# Revit family: FT6
name_source: partatom
category: Lighting Fixtures
revit_build: Autodesk Revit 2014 (Build: 20130308_1515(x64)
units: mm (PartAtom-declared; Revit-internal decimal feet)

## types (1)
- FT6
    Apparent Load = 0 VA
    Assembly Code = D5020210
    Color Filter = 16777215
    Default Elevation = 22"
    Description = 6'' Incandescent Fire-Resistant Downlights
    Dimming Lamp Color Temperature Shift = <None>
    Emit Shape Visible in Rendering = No
    Emit from Circle Diameter = 6"
    Housing Material = Steel - Hubbell
    Lamp = Incandescent
    Load Classification = Lighting
    Manufacturer = Prescolite
    Model = FT6
    Photometric Web File = generic.ies
    Power Factor = 1
    Product Documentation Link = https://hubbellcdn.com
    Product Page URL = https://www.hubbell.com
    Tilt Angle = -90.00°
    Trims = LENCES : TO64WL
    URL = https://www.hubbell.com
    Voltage = 120 V

## geometry (parser evidence)
native form markers: Blend x14, Sweep x6
no freeform markers — native parametric forms only
